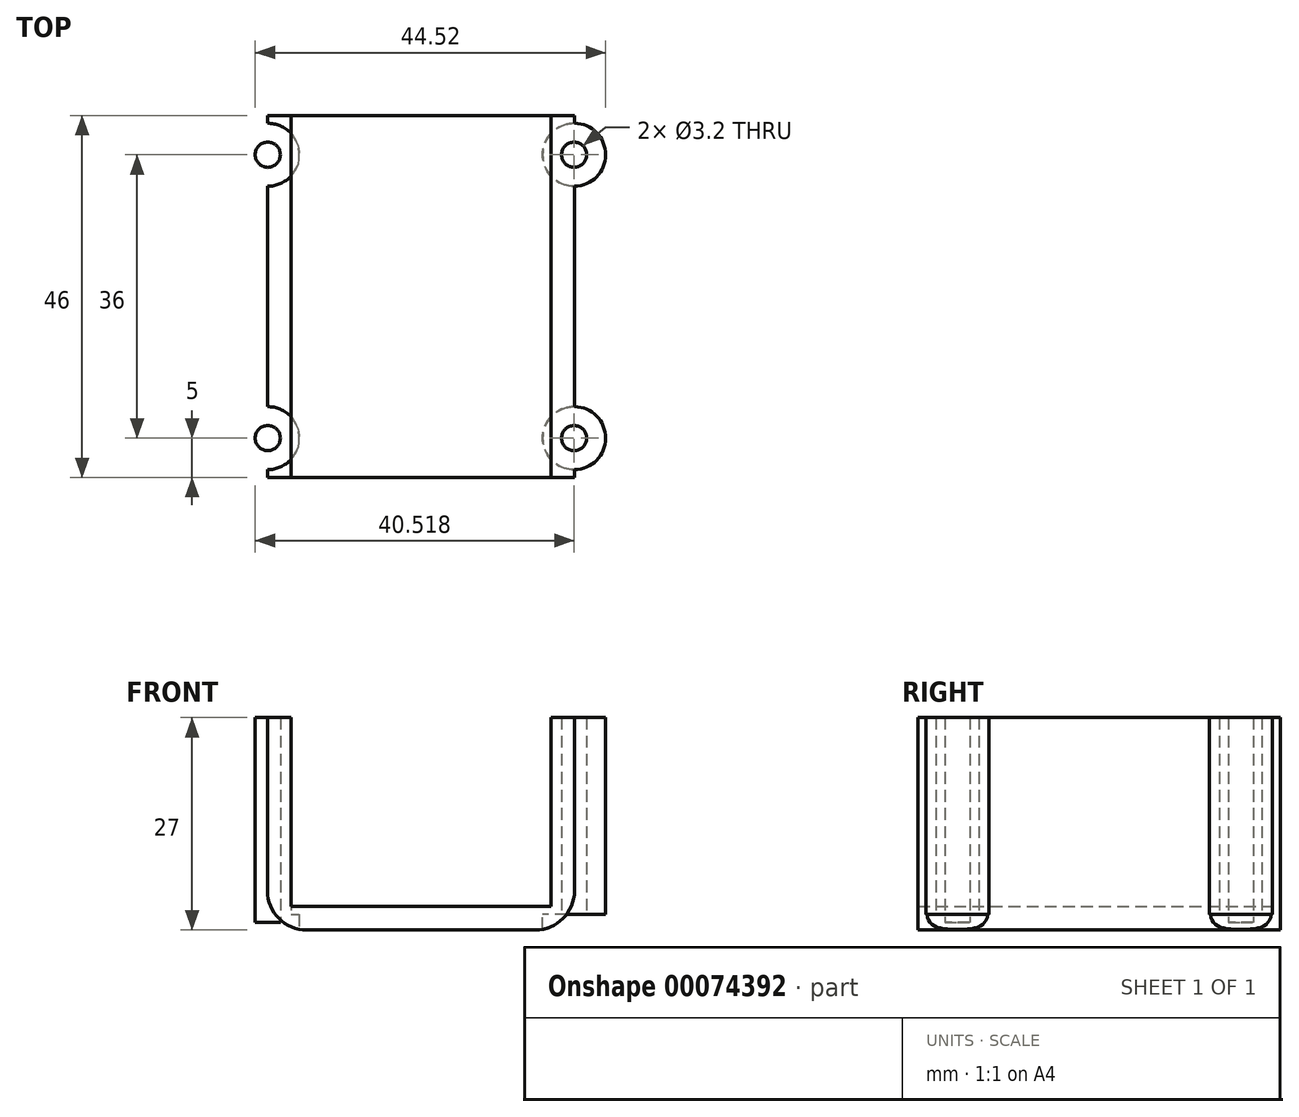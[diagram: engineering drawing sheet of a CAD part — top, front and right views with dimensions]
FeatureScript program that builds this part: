
annotation { "Feature Type Name" : "Feature", "Feature Type Description" : "" }
export const myFeature = defineFeature(function(context is Context, id is Id, definition is map)
    precondition{}
    {
        {
            var Q0;
            Q0=qCreatedBy(makeId("Front.planeOp"),FACE);
            var sketch = newSketch(context, id + "F0", { "sketchPlane" : qUnion([Q0])});
            skLineSegment(sketch, "E0.bottom", {"start": v(-16.5, 0) * mm, "end": v(16.5, 0) * mm});
            skLineSegment(sketch, "E0.left", {"start": v(-16.5, 0) * mm, "end": v(-16.5, 21) * mm});
            skLineSegment(sketch, "E0.right", {"start": v(16.5, 0) * mm, "end": v(16.5, 21) * mm});
            skLineSegment(sketch, "E1.0", {"start": v(-19.5, 24) * mm, "end": v(-16.5, 24) * mm});
            skLineSegment(sketch, "E1.1", {"start": v(-19.5, 2) * mm, "end": v(-19.5, 24) * mm});
            skLineSegment(sketch, "E1.2", {"start": v(-14.5, -3) * mm, "end": v(14.5, -3) * mm});
            skLineSegment(sketch, "E1.3", {"start": v(19.5, 2) * mm, "end": v(19.5, 24) * mm});
            skPoint(sketch, "E2.visualSharp", {"position": v(-19.5, -3) * mm});
            skArc(sketch, "E2.filletArc", {"start": v(-19.5, 2) * mm, "mid": v(-18.04, -1.54) * mm, "end": v(-14.5, -3) * mm});
            skPoint(sketch, "E3.visualSharp", {"position": v(19.5, -3) * mm});
            skArc(sketch, "E3.filletArc", {"start": v(14.5, -3) * mm, "mid": v(18.04, -1.54) * mm, "end": v(19.5, 2) * mm});
            skLineSegment(sketch, "E4", {"start": v(-16.5, 21) * mm, "end": v(-16.5, 24) * mm});
            skLineSegment(sketch, "E5", {"start": v(16.5, 21) * mm, "end": v(16.5, 24) * mm});
            skLineSegment(sketch, "E6.trimOffspring", {"start": v(16.5, 24) * mm, "end": v(19.5, 24) * mm});
            skSolve(sketch);
        }
        {
            var Q0;
            Q0=makeQuery(id+"F0.imprint","IMPRINT",FACE,{"disambiguationData":[TD([[makeQuery(id+"F0.imprint","IMPRINT",EDGE,{"derivedFrom":sQuery(id+"F0.wireOp",EDGE,"E0.bottom")}),-1.0]])]});
            extrude(context, id + "F1", {"entities" : qUnion([Q0]), "depth" : 46 * mm});
        }
        {
            var Q0;
            Q0=makeQuery(id+"F1.opExtrude","SWEPT_FACE",FACE,{"disambiguationData":[OSD([sQuery(id+"F0.wireOp",EDGE,"E1.2")])]});
            var sketch = newSketch(context, id + "F2", { "sketchPlane" : qUnion([Q0])});
            skLineSegment(sketch, "E7", {"start": v(-14.5, 23) * mm, "end": v(36.63, 23) * mm, "construction": true});
            skPoint(sketch, "E7.endSnap0", {"position": v(-14.5, 23) * mm});
            skSolve(sketch);
        }
        {
            var Q0;
            Q0=qCreatedBy(makeId("Top.planeOp"),FACE);
            var sketch = newSketch(context, id + "F3", { "sketchPlane" : qUnion([Q0])});
            skCircle(sketch, "E8", {"center": v(19.46, -5) * mm, "radius": 1.6 * mm});
            skCircle(sketch, "E9", {"center": v(19.46, -41) * mm, "radius": 1.6 * mm});
            skArc(sketch, "E10", {"start": v(16.51, -7.7) * mm, "mid": v(23.46, -5) * mm, "end": v(16.51, -2.3) * mm});
            skArc(sketch, "E11", {"start": v(16.51, -43.7) * mm, "mid": v(23.46, -41) * mm, "end": v(16.51, -38.3) * mm});
            skLineSegment(sketch, "E12", {"start": v(16.51, -2.3) * mm, "end": v(16.51, -7.7) * mm});
            skLineSegment(sketch, "E13.trimOffspring", {"start": v(16.51, -38.3) * mm, "end": v(16.51, -43.7) * mm});
            skCircle(sketch, "E14.MirrorC", {"center": v(-19.46, -5) * mm, "radius": 1.6 * mm});
            skCircle(sketch, "E15.MirrorC", {"center": v(-19.46, -41) * mm, "radius": 1.6 * mm});
            skArc(sketch, "E16.MirrorCS", {"start": v(-16.51, -7.7) * mm, "mid": v(-23.46, -5) * mm, "end": v(-16.51, -2.3) * mm});
            skArc(sketch, "E17.MirrorCS", {"start": v(-16.51, -43.7) * mm, "mid": v(-23.46, -41) * mm, "end": v(-16.51, -38.3) * mm});
            skLineSegment(sketch, "E18.MirrorCS", {"start": v(-16.51, -38.3) * mm, "end": v(-16.51, -43.7) * mm});
            skLineSegment(sketch, "E19.MirrorCS", {"start": v(-16.51, -2.3) * mm, "end": v(-16.51, -7.7) * mm});
            skArc(sketch, "E20", {"start": v(-16.51, -43.7) * mm, "mid": v(-15.46, -41) * mm, "end": v(-16.51, -38.3) * mm});
            skArc(sketch, "E21.MirrorCS", {"start": v(16.51, -43.7) * mm, "mid": v(15.46, -41) * mm, "end": v(16.51, -38.3) * mm});
            skArc(sketch, "E22.MirrorCS", {"start": v(-16.51, -2.3) * mm, "mid": v(-15.46, -5) * mm, "end": v(-16.51, -7.7) * mm});
            skArc(sketch, "E23.MirrorCS", {"start": v(16.51, -2.3) * mm, "mid": v(15.46, -5) * mm, "end": v(16.51, -7.7) * mm});
            skSolve(sketch);
        }
        {
            var Q0;
            Q0=makeQuery(id+"F3.imprint","IMPRINT",FACE,{"disambiguationData":[TD([[makeQuery(id+"F3.imprint","IMPRINT",EDGE,{"derivedFrom":sQuery(id+"F3.wireOp",EDGE,"E14.MirrorC")}),1.0]])]});
            var Q1;
            Q1=makeQuery(id+"F3.imprint","IMPRINT",FACE,{"disambiguationData":[TD([[makeQuery(id+"F3.imprint","IMPRINT",EDGE,{"derivedFrom":sQuery(id+"F3.wireOp",EDGE,"E8")}),-1.0]])]});
            var Q2;
            Q2=makeQuery(id+"F3.imprint","IMPRINT",FACE,{"disambiguationData":[TD([[makeQuery(id+"F3.imprint","IMPRINT",EDGE,{"derivedFrom":sQuery(id+"F3.wireOp",EDGE,"E9")}),-1.0]])]});
            var Q3;
            Q3=makeQuery(id+"F3.imprint","IMPRINT",FACE,{"disambiguationData":[TD([[makeQuery(id+"F3.imprint","IMPRINT",EDGE,{"derivedFrom":sQuery(id+"F3.wireOp",EDGE,"E15.MirrorC")}),1.0]])]});
            var Q4;
            Q4=makeQuery(id+"F1.opExtrude","SWEPT_FACE",FACE,{"disambiguationData":[OSD([sQuery(id+"F0.wireOp",EDGE,"E1.0")])]});
            extrude(context, id + "F4", {"entities" : qUnion([Q0, Q1, Q2, Q3]), "operationType" : NewBodyOperationType.ADD, "endBound" : BoundingType.UP_TO_SURFACE, "endBoundEntityFace" : qUnion([Q4]), "depth" : 25 * mm});
        }
        {
            var Q0;
            Q0=makeQuery(id+"F3.imprint","IMPRINT",FACE,{"disambiguationData":[TD([[makeQuery(id+"F3.imprint","IMPRINT",EDGE,{"derivedFrom":sQuery(id+"F3.wireOp",EDGE,"E8")}),1.0]])]});
            var Q1;
            Q1=makeQuery(id+"F3.imprint","IMPRINT",FACE,{"disambiguationData":[TD([[makeQuery(id+"F3.imprint","IMPRINT",EDGE,{"derivedFrom":sQuery(id+"F3.wireOp",EDGE,"E14.MirrorC")}),-1.0]])]});
            var Q2;
            Q2=makeQuery(id+"F3.imprint","IMPRINT",FACE,{"disambiguationData":[TD([[makeQuery(id+"F3.imprint","IMPRINT",EDGE,{"derivedFrom":sQuery(id+"F3.wireOp",EDGE,"E15.MirrorC")}),-1.0]])]});
            var Q3;
            Q3=makeQuery(id+"F3.imprint","IMPRINT",FACE,{"disambiguationData":[TD([[makeQuery(id+"F3.imprint","IMPRINT",EDGE,{"derivedFrom":sQuery(id+"F3.wireOp",EDGE,"E9")}),1.0]])]});
            extrude(context, id + "F5", {"entities" : qUnion([Q0, Q1, Q2, Q3]), "operationType" : NewBodyOperationType.REMOVE, "endBound" : BoundingType.THROUGH_ALL, "depth" : 25 * mm, "hasSecondDirection" : true, "secondDirectionBound" : SecondDirectionBoundingType.THROUGH_ALL, "secondDirectionOppositeDirection" : true, "secondDirectionDepth" : 25 * mm});
        }
        {
            var Q0;
            Q0=makeQuery(id+"F3.imprint","IMPRINT",FACE,{"disambiguationData":[TD([[makeQuery(id+"F3.imprint","IMPRINT",EDGE,{"derivedFrom":sQuery(id+"F3.wireOp",EDGE,"E8")}),-1.0]])]});
            var Q1;
            Q1=makeQuery(id+"F3.imprint","IMPRINT",FACE,{"disambiguationData":[TD([[makeQuery(id+"F3.imprint","IMPRINT",EDGE,{"derivedFrom":sQuery(id+"F3.wireOp",EDGE,"E14.MirrorC")}),1.0]])]});
            var Q2;
            Q2=makeQuery(id+"F3.imprint","IMPRINT",FACE,{"disambiguationData":[TD([[makeQuery(id+"F3.imprint","IMPRINT",EDGE,{"derivedFrom":sQuery(id+"F3.wireOp",EDGE,"E9")}),-1.0]])]});
            extrude(context, id + "F6", {"entities" : qUnion([Q0, Q1, Q2]), "operationType" : NewBodyOperationType.REMOVE, "oppositeDirection" : true, "depth" : 25 * mm});
        }
        {
            var Q0;
            Q0=makeQuery(id+"F3.imprint","IMPRINT",FACE,{"disambiguationData":[TD([[makeQuery(id+"F3.imprint","IMPRINT",EDGE,{"derivedFrom":sQuery(id+"F3.wireOp",EDGE,"E15.MirrorC")}),1.0]])]});
            var Q1;
            Q1=makeQuery(id+"F3.imprint","IMPRINT",FACE,{"disambiguationData":[TD([[makeQuery(id+"F3.imprint","IMPRINT",EDGE,{"derivedFrom":sQuery(id+"F3.wireOp",EDGE,"E14.MirrorC")}),1.0]])]});
            var Q2;
            Q2=makeQuery(id+"F3.imprint","IMPRINT",FACE,{"disambiguationData":[TD([[makeQuery(id+"F3.imprint","IMPRINT",EDGE,{"derivedFrom":sQuery(id+"F3.wireOp",EDGE,"E9")}),-1.0]])]});
            var Q3;
            Q3=makeQuery(id+"F3.imprint","IMPRINT",FACE,{"disambiguationData":[TD([[makeQuery(id+"F3.imprint","IMPRINT",EDGE,{"derivedFrom":sQuery(id+"F3.wireOp",EDGE,"E8")}),-1.0]])]});
            extrude(context, id + "F7", {"entities" : qUnion([Q0, Q1, Q2, Q3]), "operationType" : NewBodyOperationType.ADD, "oppositeDirection" : true, "depth" : 2 * mm});
        }
        {
            var Q0;
            Q0 = qSketchRegion(id + "F3", true);
            extrude(context, id + "F8", {"entities" : qUnion([Q0]), "operationType" : NewBodyOperationType.REMOVE, "oppositeDirection" : true, "depth" : 25 * mm});
        }
        {
            var Q0;
            Q0=makeQuery(id+"F3.imprint","IMPRINT",FACE,{"disambiguationData":[TD([[makeQuery(id+"F3.imprint","IMPRINT",EDGE,{"derivedFrom":sQuery(id+"F3.wireOp",EDGE,"E18.MirrorCS")}),1.0]])]});
            var Q1;
            Q1=makeQuery(id+"F3.imprint","IMPRINT",FACE,{"disambiguationData":[TD([[makeQuery(id+"F3.imprint","IMPRINT",EDGE,{"derivedFrom":sQuery(id+"F3.wireOp",EDGE,"E15.MirrorC")}),1.0]])]});
            var Q2;
            Q2=makeQuery(id+"F3.imprint","IMPRINT",FACE,{"disambiguationData":[TD([[makeQuery(id+"F3.imprint","IMPRINT",EDGE,{"derivedFrom":sQuery(id+"F3.wireOp",EDGE,"E13.trimOffspring")}),-1.0]])]});
            var Q3;
            Q3=makeQuery(id+"F3.imprint","IMPRINT",FACE,{"disambiguationData":[TD([[makeQuery(id+"F3.imprint","IMPRINT",EDGE,{"derivedFrom":sQuery(id+"F3.wireOp",EDGE,"E9")}),-1.0]])]});
            var Q4;
            Q4=makeQuery(id+"F3.imprint","IMPRINT",FACE,{"disambiguationData":[TD([[makeQuery(id+"F3.imprint","IMPRINT",EDGE,{"derivedFrom":sQuery(id+"F3.wireOp",EDGE,"E12")}),-1.0]])]});
            var Q5;
            Q5=makeQuery(id+"F3.imprint","IMPRINT",FACE,{"disambiguationData":[TD([[makeQuery(id+"F3.imprint","IMPRINT",EDGE,{"derivedFrom":sQuery(id+"F3.wireOp",EDGE,"E8")}),-1.0]])]});
            var Q6;
            Q6=makeQuery(id+"F3.imprint","IMPRINT",FACE,{"disambiguationData":[TD([[makeQuery(id+"F3.imprint","IMPRINT",EDGE,{"derivedFrom":sQuery(id+"F3.wireOp",EDGE,"E19.MirrorCS")}),1.0]])]});
            var Q7;
            Q7=makeQuery(id+"F3.imprint","IMPRINT",FACE,{"disambiguationData":[TD([[makeQuery(id+"F3.imprint","IMPRINT",EDGE,{"derivedFrom":sQuery(id+"F3.wireOp",EDGE,"E14.MirrorC")}),1.0]])]});
            extrude(context, id + "F9", {"entities" : qUnion([Q0, Q1, Q2, Q3, Q4, Q5, Q6, Q7]), "operationType" : NewBodyOperationType.ADD, "oppositeDirection" : true, "depth" : 1 * mm});
        }
    });
